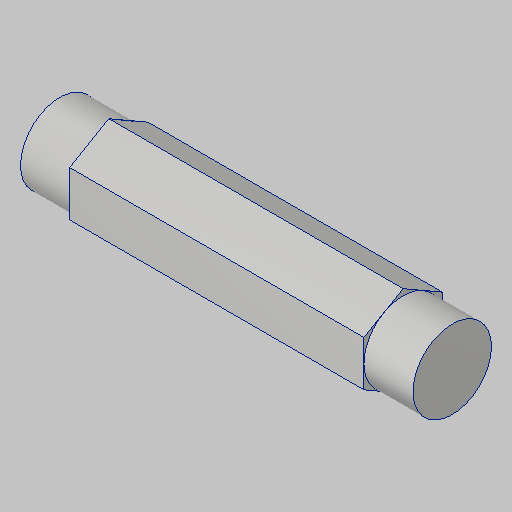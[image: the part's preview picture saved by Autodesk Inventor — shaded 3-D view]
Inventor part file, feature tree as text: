
AUTODESK INVENTOR PART (.ipt)
format: ipt  version: 2023.5 (Build 275446000, 446)  size: 265,728 bytes
history: native  units: in
note: dims shown in document units (in); Inventor stores cm internally (conversion verified against a paired STEP export)
features: extrude x3, sketch x3, projected_geometry x2
ambient origin geometry x8: Origin, YZ Plane, XZ Plane, XY Plane, X Axis, Y Axis, Z Axis, Center Point
bodies: Solid1 (feature_tree)
feature tree (8):
  extrude  "Extrusion1"  Depth=2.5in TaperAngle=0.0deg
  extrude  "Extrusion2"  Depth=0.3125in TaperAngle=0.0deg
  extrude  "Extrusion3"  Depth=0.3125in TaperAngle=0.0deg
  sketch  "Sketch1"  dims[d0=0.5in d1=2.5in d2=0.0in]
  sketch  "Sketch2"  dims[d3=0.5in d4=0.3125in d5=0.0in]
  projected_geometry  "Projected Loop1"
  sketch  "Sketch3"  dims[d6=0.5in d7=0.3125in d8=0.0in]
  projected_geometry  "Projected Loop2"
